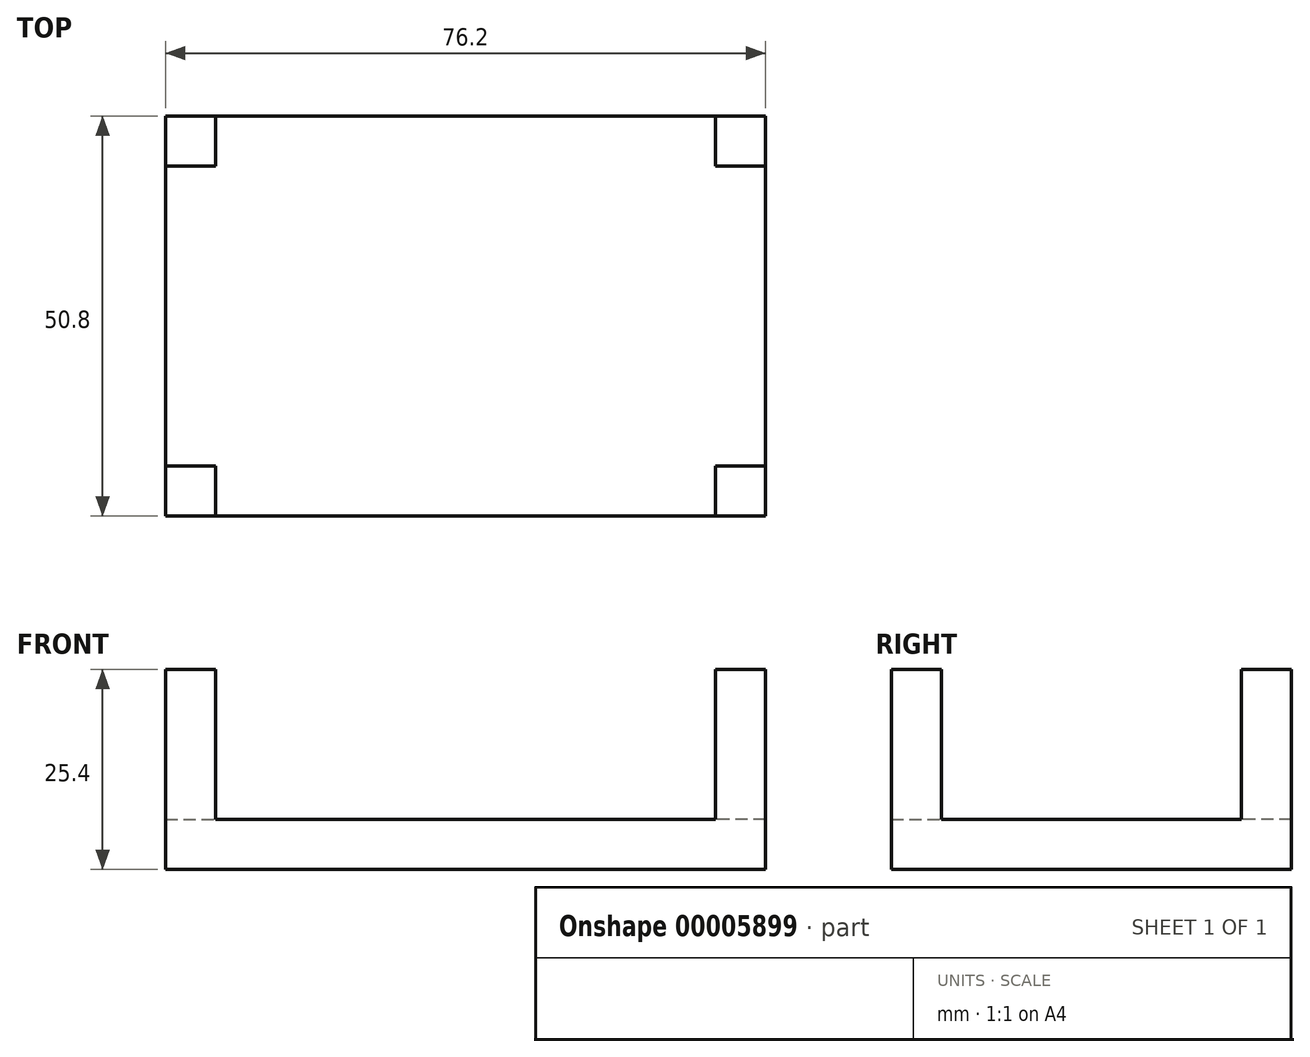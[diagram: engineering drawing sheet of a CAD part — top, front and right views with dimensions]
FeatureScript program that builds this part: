
annotation { "Feature Type Name" : "Feature", "Feature Type Description" : "" }
export const myFeature = defineFeature(function(context is Context, id is Id, definition is map)
    precondition{}
    {
        {
            var Q0;
            Q0=qCreatedBy(makeId("Top.planeOp"),FACE);
            var sketch = newSketch(context, id + "F0", { "sketchPlane" : qUnion([Q0])});
            skLineSegment(sketch, "E0.rect.bottom", {"start": v(38.1, 25.4) * mm, "end": v(-38.1, 25.4) * mm});
            skLineSegment(sketch, "E0.rect.top", {"start": v(38.1, -25.4) * mm, "end": v(-38.1, -25.4) * mm});
            skLineSegment(sketch, "E0.rect.left", {"start": v(38.1, 25.4) * mm, "end": v(38.1, -25.4) * mm});
            skLineSegment(sketch, "E0.rect.right", {"start": v(-38.1, 25.4) * mm, "end": v(-38.1, -25.4) * mm});
            skPoint(sketch, "E0.rect.middle", {"position": v(0, 0) * mm});
            skSolve(sketch);
        }
        {
            var Q0;
            Q0=makeQuery(id+"F0.imprint","IMPRINT",FACE,{"disambiguationData":[TD([[makeQuery(id+"F0.imprint","IMPRINT",EDGE,{"derivedFrom":sQuery(id+"F0.wireOp",EDGE,"E0.rect.bottom")}),1.0]])]});
            extrude(context, id + "F1", {"entities" : qUnion([Q0]), "depth" : 6.35 * mm});
        }
        {
            var Q0;
            Q0=makeQuery(id+"F1.opExtrude","CAP_FACE",FACE,{"disambiguationData":[OSD([sQuery(id+"F0.wireOp",EDGE,"E0.rect.bottom"),sQuery(id+"F0.wireOp",EDGE,"E0.rect.top"),sQuery(id+"F0.wireOp",EDGE,"E0.rect.left"),sQuery(id+"F0.wireOp",EDGE,"E0.rect.right")])],"isStart":false});
            var sketch = newSketch(context, id + "F2", { "sketchPlane" : qUnion([Q0])});
            skLineSegment(sketch, "E1.bottom", {"start": v(-38.1, 25.4) * mm, "end": v(-31.75, 25.4) * mm});
            skLineSegment(sketch, "E1.top", {"start": v(-38.1, 19.05) * mm, "end": v(-31.75, 19.05) * mm});
            skLineSegment(sketch, "E1.left", {"start": v(-38.1, 25.4) * mm, "end": v(-38.1, 19.05) * mm});
            skLineSegment(sketch, "E1.right", {"start": v(-31.75, 25.4) * mm, "end": v(-31.75, 19.05) * mm});
            skLineSegment(sketch, "E2.bottom", {"start": v(38.1, 25.4) * mm, "end": v(31.75, 25.4) * mm});
            skLineSegment(sketch, "E2.top", {"start": v(38.1, 19.05) * mm, "end": v(31.75, 19.05) * mm});
            skLineSegment(sketch, "E2.left", {"start": v(38.1, 25.4) * mm, "end": v(38.1, 19.05) * mm});
            skLineSegment(sketch, "E2.right", {"start": v(31.75, 25.4) * mm, "end": v(31.75, 19.05) * mm});
            skLineSegment(sketch, "E3.bottom", {"start": v(38.1, -25.4) * mm, "end": v(31.75, -25.4) * mm});
            skLineSegment(sketch, "E3.top", {"start": v(38.1, -19.05) * mm, "end": v(31.75, -19.05) * mm});
            skLineSegment(sketch, "E3.left", {"start": v(38.1, -25.4) * mm, "end": v(38.1, -19.05) * mm});
            skLineSegment(sketch, "E3.right", {"start": v(31.75, -25.4) * mm, "end": v(31.75, -19.05) * mm});
            skLineSegment(sketch, "E4.bottom", {"start": v(-38.1, -25.4) * mm, "end": v(-31.75, -25.4) * mm});
            skLineSegment(sketch, "E4.top", {"start": v(-38.1, -19.05) * mm, "end": v(-31.75, -19.05) * mm});
            skLineSegment(sketch, "E4.left", {"start": v(-38.1, -25.4) * mm, "end": v(-38.1, -19.05) * mm});
            skLineSegment(sketch, "E4.right", {"start": v(-31.75, -25.4) * mm, "end": v(-31.75, -19.05) * mm});
            skSolve(sketch);
        }
        {
            var Q0;
            Q0=makeQuery(id+"F2.imprint","IMPRINT",FACE,{"disambiguationData":[TD([[makeQuery(id+"F2.imprint","IMPRINT",EDGE,{"derivedFrom":sQuery(id+"F2.wireOp",EDGE,"E1.bottom")}),1.0]])]});
            var Q1;
            Q1=makeQuery(id+"F2.imprint","IMPRINT",FACE,{"disambiguationData":[TD([[makeQuery(id+"F2.imprint","IMPRINT",EDGE,{"derivedFrom":sQuery(id+"F2.wireOp",EDGE,"E2.bottom")}),1.0]])]});
            var Q2;
            Q2=makeQuery(id+"F2.imprint","IMPRINT",FACE,{"disambiguationData":[TD([[makeQuery(id+"F2.imprint","IMPRINT",EDGE,{"derivedFrom":sQuery(id+"F2.wireOp",EDGE,"E3.bottom")}),-1.0]])]});
            var Q3;
            Q3=makeQuery(id+"F2.imprint","IMPRINT",FACE,{"disambiguationData":[TD([[makeQuery(id+"F2.imprint","IMPRINT",EDGE,{"derivedFrom":sQuery(id+"F2.wireOp",EDGE,"E4.bottom")}),-1.0]])]});
            extrude(context, id + "F3", {"entities" : qUnion([Q0, Q1, Q2, Q3]), "operationType" : NewBodyOperationType.ADD, "depth" : 19.05 * mm});
        }
    });
